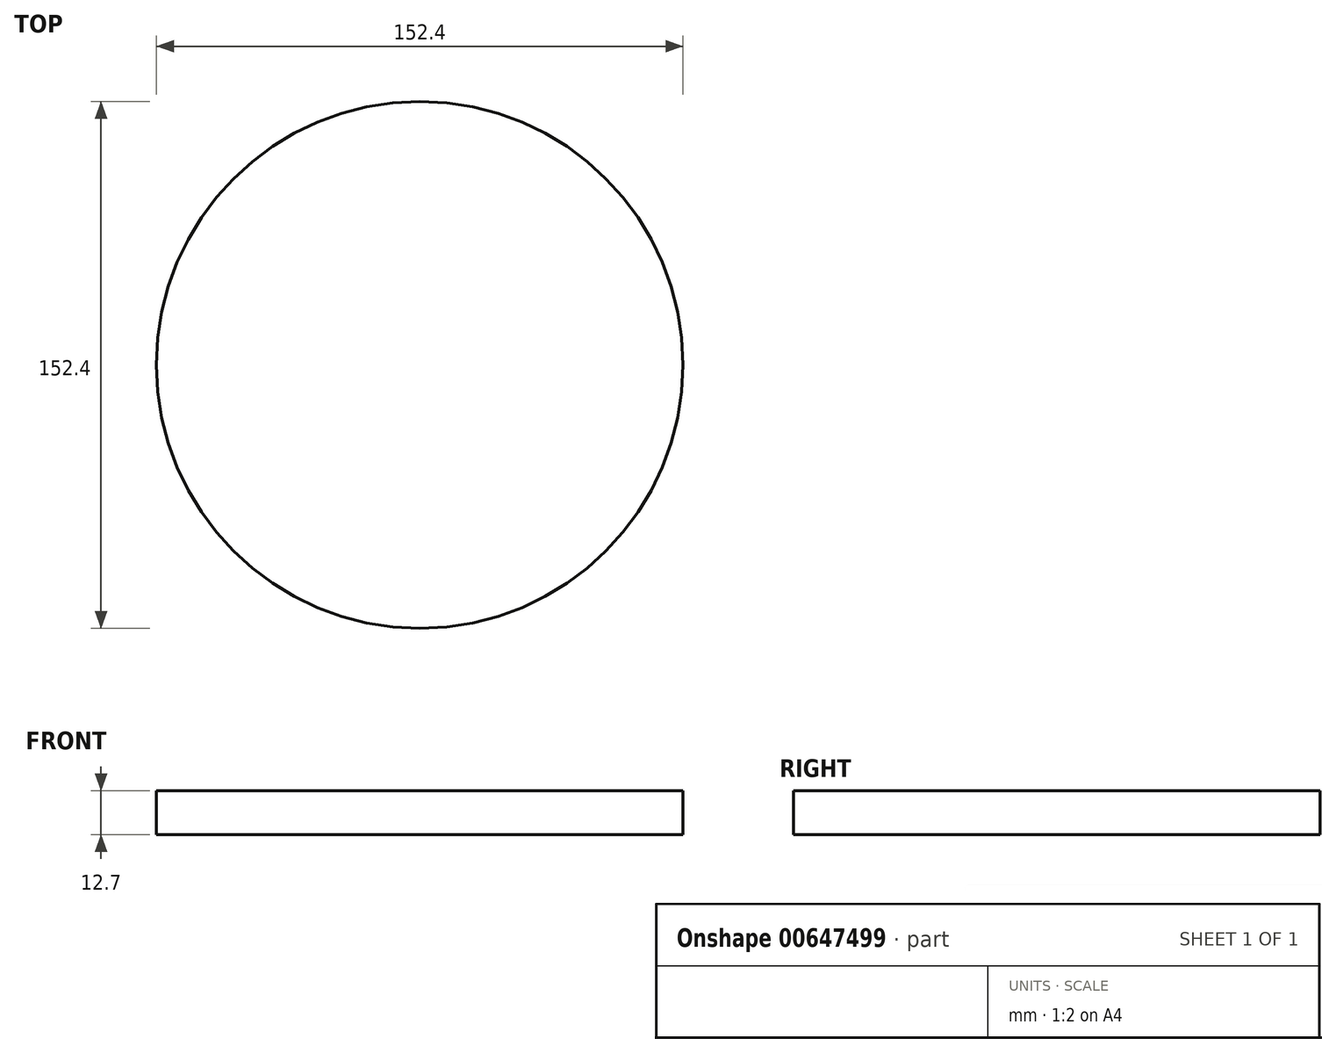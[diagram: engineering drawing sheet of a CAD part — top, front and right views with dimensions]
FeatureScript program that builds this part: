
annotation { "Feature Type Name" : "Feature", "Feature Type Description" : "" }
export const myFeature = defineFeature(function(context is Context, id is Id, definition is map)
    precondition{}
    {
        {
            var Q0;
            Q0=qCreatedBy(makeId("Top.planeOp"),FACE);
            var sketch = newSketch(context, id + "F0", { "sketchPlane" : qUnion([Q0])});
            skCircle(sketch, "E0", {"center": v(0, 0) * mm, "radius": 76.2 * mm});
            skSolve(sketch);
        }
        {
            var Q0;
            Q0=qSketchRegion(id+"F0",true);
            extrude(context, id + "F1", {"entities" : qUnion([Q0]), "depth" : 12.7 * mm});
        }
    });
